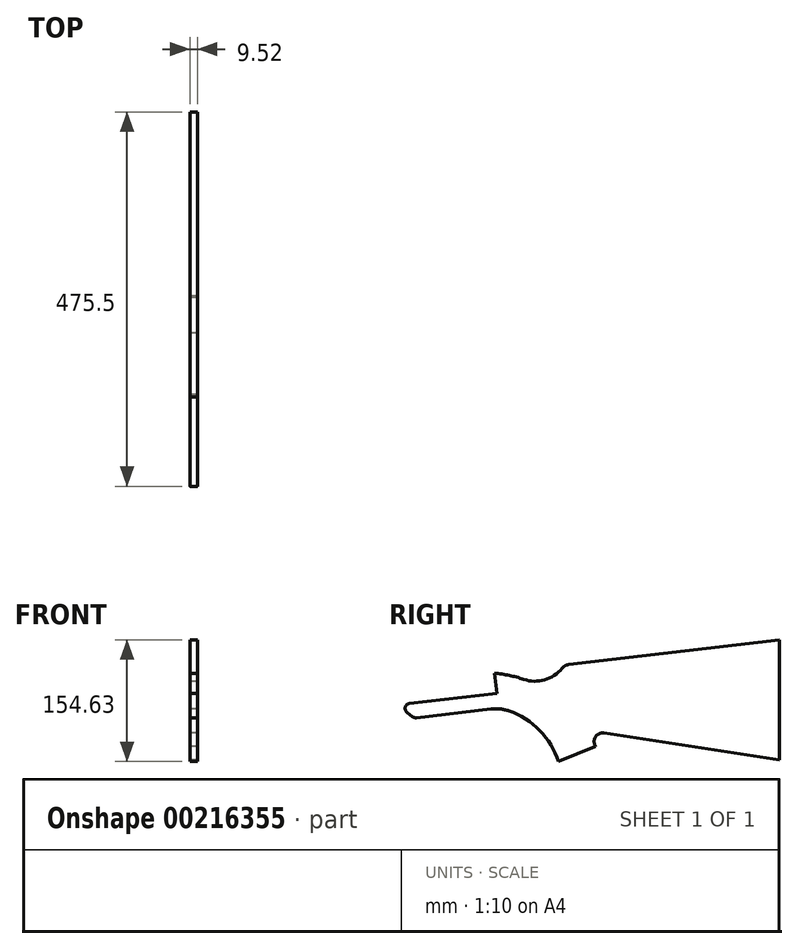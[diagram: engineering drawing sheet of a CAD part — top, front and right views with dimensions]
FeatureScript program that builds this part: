
annotation { "Feature Type Name" : "Feature", "Feature Type Description" : "" }
export const myFeature = defineFeature(function(context is Context, id is Id, definition is map)
    precondition{}
    {
        {
            var Q0;
            Q0=qCreatedBy(makeId("Right.planeOp"),FACE);
            var sketch = newSketch(context, id + "F0", { "sketchPlane" : qUnion([Q0])});
            skLineSegment(sketch, "E0", {"start": v(178.65, 74.14) * mm, "end": v(178.65, -78.26) * mm});
            skLineSegment(sketch, "E1", {"start": v(178.65, 74.14) * mm, "end": v(-89.03, 42.68) * mm});
            skLineSegment(sketch, "E2", {"start": v(-183.3, 31.6) * mm, "end": v(-180.34, 6.37) * mm});
            skLineSegment(sketch, "E3", {"start": v(-101.91, -80.5) * mm, "end": v(-54.82, -61.44) * mm});
            skArc(sketch, "E4", {"start": v(-44.11, -44.26) * mm, "mid": v(-55.13, -49.32) * mm, "end": v(-54.82, -61.44) * mm});
            skLineSegment(sketch, "E5", {"start": v(-44.11, -44.26) * mm, "end": v(178.65, -78.26) * mm});
            skArc(sketch, "E6", {"start": v(-101.91, -80.5) * mm, "mid": v(-125.92, -40.97) * mm, "end": v(-164.96, -16.17) * mm});
            skArc(sketch, "E7", {"start": v(-54.82, -61.44) * mm, "mid": v(-55.67, -59.46) * mm, "end": v(-56.54, -57.49) * mm});
            skArc(sketch, "E8", {"start": v(-146.28, 23.95) * mm, "mid": v(-119.63, 23.32) * mm, "end": v(-97.42, 38.06) * mm});
            skArc(sketch, "E9", {"start": v(-89.03, 42.68) * mm, "mid": v(-93.68, 41.19) * mm, "end": v(-97.42, 38.06) * mm});
            skLineSegment(sketch, "E10", {"start": v(-183.3, 31.6) * mm, "end": v(-280.41, 20.18) * mm, "construction": true});
            skLineSegment(sketch, "E11", {"start": v(-180.34, 6.37) * mm, "end": v(-291.24, -6.66) * mm});
            skLineSegment(sketch, "E12", {"start": v(-294.44, -17.95) * mm, "end": v(-287.39, -23.52) * mm});
            skLineSegment(sketch, "E13", {"start": v(-282.71, -24.84) * mm, "end": v(-187.69, -13.67) * mm});
            skPoint(sketch, "E14.visualSharp", {"position": v(-306.47, -8.45) * mm});
            skArc(sketch, "E14.filletArc", {"start": v(-291.24, -6.66) * mm, "mid": v(-296.61, -11.24) * mm, "end": v(-294.44, -17.95) * mm});
            skPoint(sketch, "E15.visualSharp", {"position": v(-285.32, -25.15) * mm});
            skArc(sketch, "E15.filletArc", {"start": v(-287.39, -23.52) * mm, "mid": v(-285.18, -24.65) * mm, "end": v(-282.71, -24.84) * mm});
            skArc(sketch, "E16", {"start": v(-164.96, -16.17) * mm, "mid": v(-176.18, -13.63) * mm, "end": v(-187.69, -13.67) * mm});
            skPoint(sketch, "E17.orphan", {"position": v(-178.11, -12.55) * mm});
            skArc(sketch, "E18.trimOffspring", {"start": v(-146.28, 23.95) * mm, "mid": v(-164.56, 28.93) * mm, "end": v(-183.3, 31.6) * mm});
            skSolve(sketch);
        }
        {
            var Q0;
            Q0=makeQuery(id+"F0.imprint","IMPRINT",FACE,{"disambiguationData":[TD([[makeQuery(id+"F0.imprint","IMPRINT",EDGE,{"derivedFrom":sQuery(id+"F0.wireOp",EDGE,"E0")}),-1.0]])]});
            extrude(context, id + "F1", {"entities" : qUnion([Q0]), "endBound" : BoundingType.SYMMETRIC, "depth" : 9.52 * mm});
        }
    });
